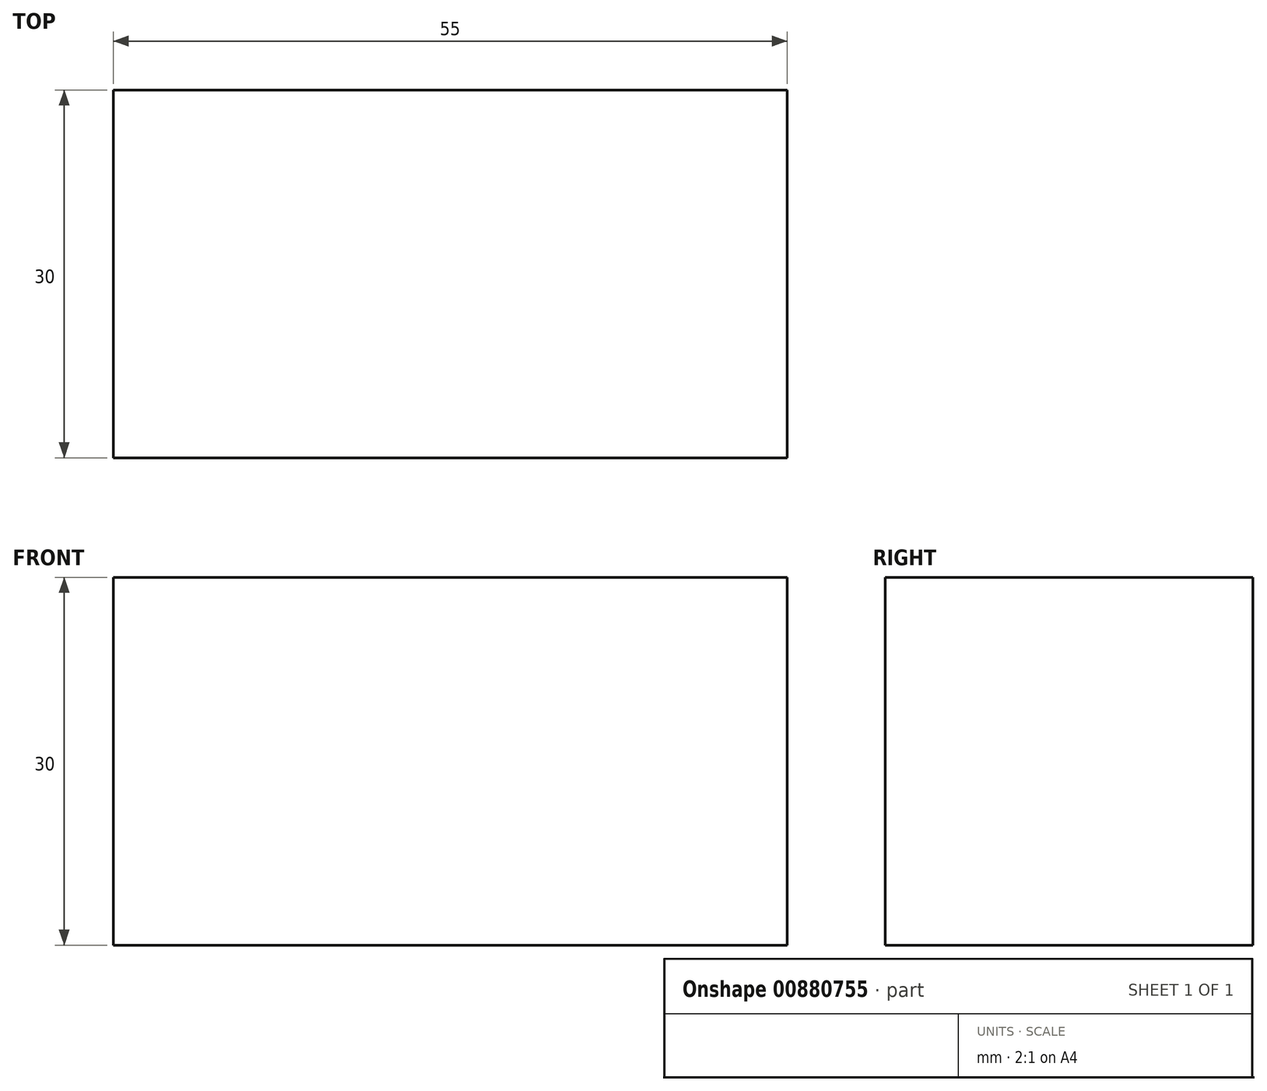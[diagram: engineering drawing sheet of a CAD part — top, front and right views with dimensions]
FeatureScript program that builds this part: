
annotation { "Feature Type Name" : "Feature", "Feature Type Description" : "" }
export const myFeature = defineFeature(function(context is Context, id is Id, definition is map)
    precondition{}
    {
        {
            var Q0;
            Q0=qCreatedBy(makeId("Top.planeOp"),FACE);
            var sketch = newSketch(context, id + "F0", { "sketchPlane" : qUnion([Q0])});
            skLineSegment(sketch, "E0.bottom", {"start": v(27.5, -15) * mm, "end": v(-27.5, -15) * mm});
            skLineSegment(sketch, "E0.top", {"start": v(27.5, 15) * mm, "end": v(-27.5, 15) * mm});
            skLineSegment(sketch, "E0.left", {"start": v(27.5, -15) * mm, "end": v(27.5, 15) * mm});
            skLineSegment(sketch, "E0.right", {"start": v(-27.5, -15) * mm, "end": v(-27.5, 15) * mm});
            skPoint(sketch, "E0.middle", {"position": v(0, 0) * mm});
            skSolve(sketch);
        }
        {
            var Q0;
            Q0 = qSketchRegion(id + "F0", true);
            extrude(context, id + "F1", {"entities" : qUnion([Q0]), "depth" : 30 * mm, "offsetDistance" : 25 * mm});
        }
    });
